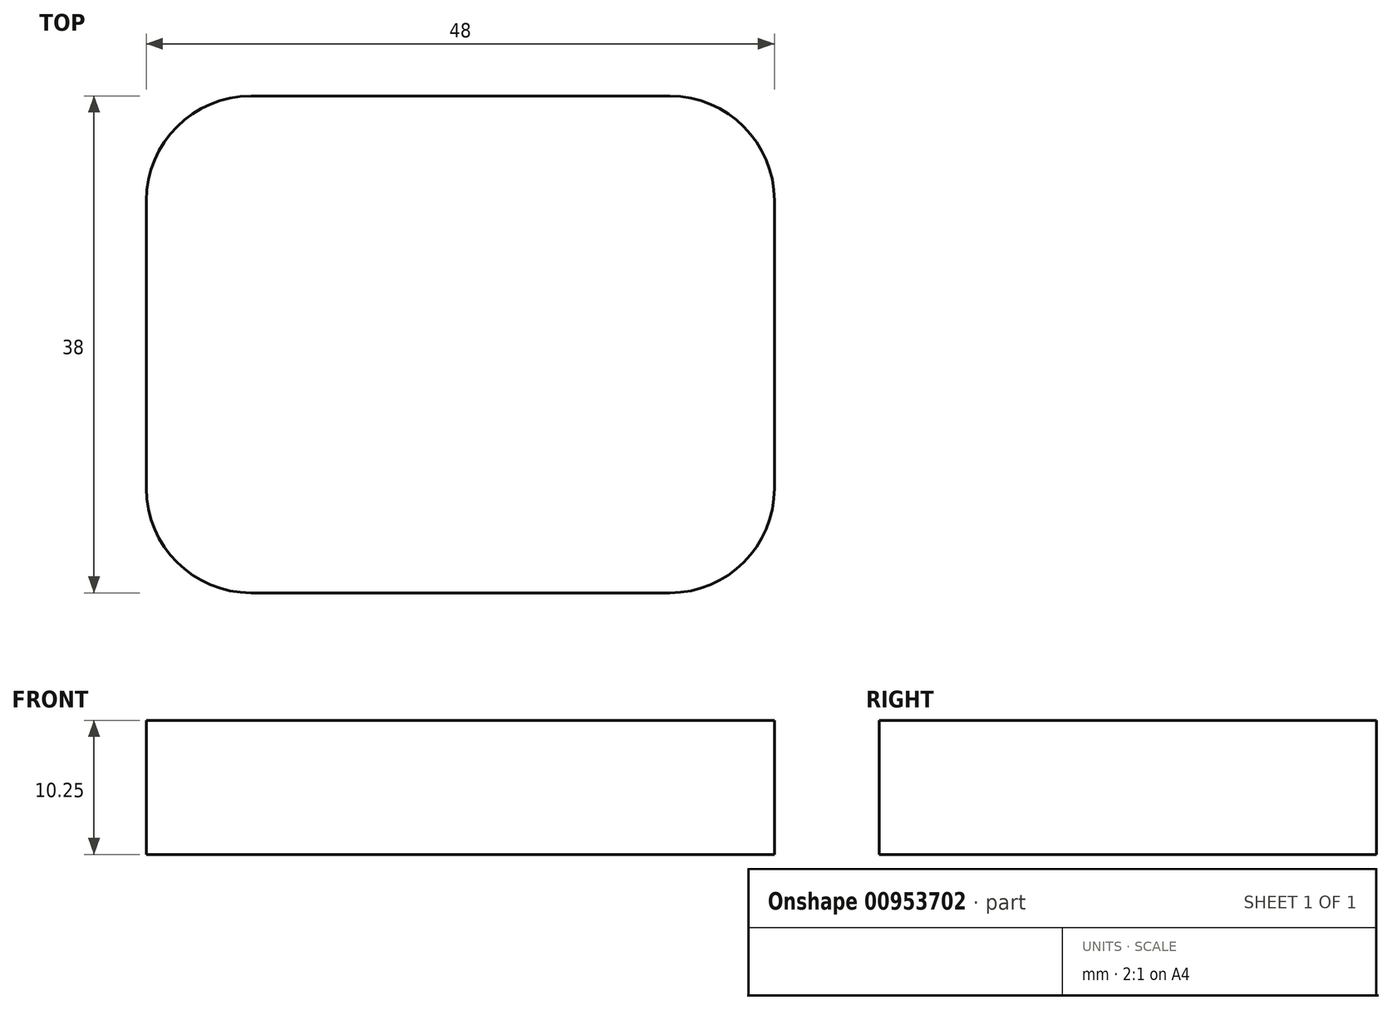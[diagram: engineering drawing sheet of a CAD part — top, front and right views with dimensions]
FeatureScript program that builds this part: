
annotation { "Feature Type Name" : "Feature", "Feature Type Description" : "" }
export const myFeature = defineFeature(function(context is Context, id is Id, definition is map)
    precondition{}
    {
        {
            var Q0;
            Q0=qCreatedBy(makeId("Top.planeOp"),FACE);
            var sketch = newSketch(context, id + "F0", { "sketchPlane" : qUnion([Q0])});
            skLineSegment(sketch, "E0.bottom", {"start": v(-16, 19) * mm, "end": v(16, 19) * mm});
            skLineSegment(sketch, "E0.top", {"start": v(-16, -19) * mm, "end": v(16, -19) * mm});
            skLineSegment(sketch, "E0.left", {"start": v(-24, 11) * mm, "end": v(-24, -11) * mm});
            skLineSegment(sketch, "E0.right", {"start": v(24, 11) * mm, "end": v(24, -11) * mm});
            skPoint(sketch, "E1.visualSharp", {"position": v(-24, 19) * mm});
            skArc(sketch, "E1.filletArc", {"start": v(-16, 19) * mm, "mid": v(-21.66, 16.66) * mm, "end": v(-24, 11) * mm});
            skPoint(sketch, "E2.visualSharp", {"position": v(-24, -19) * mm});
            skArc(sketch, "E2.filletArc", {"start": v(-24, -11) * mm, "mid": v(-21.66, -16.66) * mm, "end": v(-16, -19) * mm});
            skPoint(sketch, "E3.visualSharp", {"position": v(24, -19) * mm});
            skArc(sketch, "E3.filletArc", {"start": v(16, -19) * mm, "mid": v(21.66, -16.66) * mm, "end": v(24, -11) * mm});
            skPoint(sketch, "E4.visualSharp", {"position": v(24, 19) * mm});
            skArc(sketch, "E4.filletArc", {"start": v(24, 11) * mm, "mid": v(21.66, 16.66) * mm, "end": v(16, 19) * mm});
            skSolve(sketch);
        }
        {
            var Q0;
            Q0 = qSketchRegion(id + "F0", true);
            extrude(context, id + "F1", {"entities" : qUnion([Q0]), "depth" : 10.25 * mm, "offsetDistance" : 25 * mm});
        }
    });
